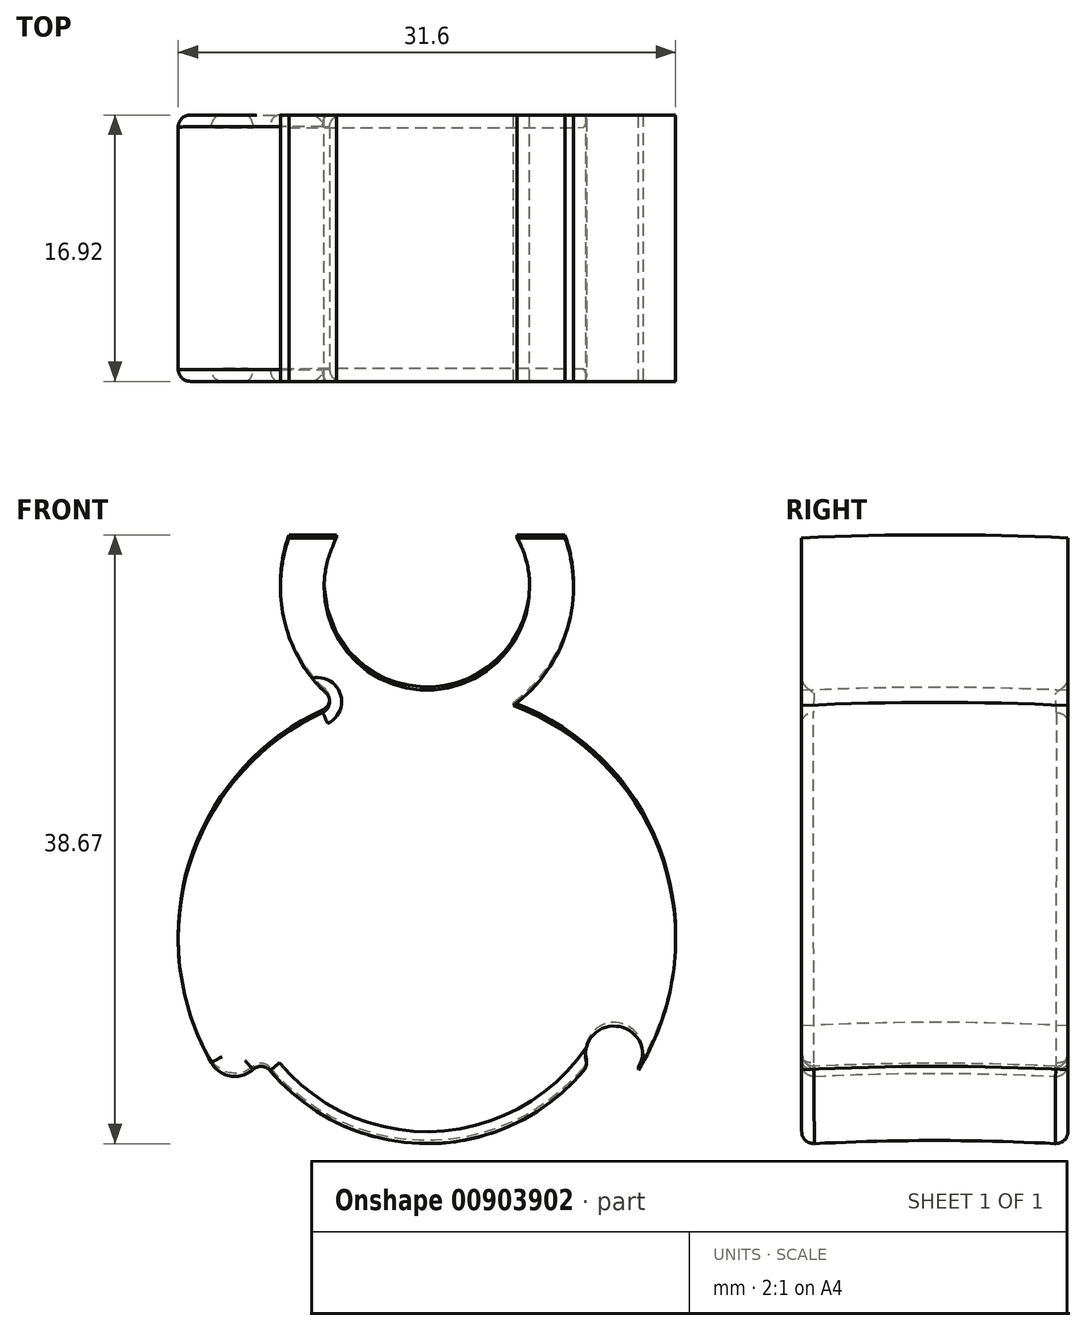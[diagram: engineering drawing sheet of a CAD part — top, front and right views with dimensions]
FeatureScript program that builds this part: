
annotation { "Feature Type Name" : "Feature", "Feature Type Description" : "" }
export const myFeature = defineFeature(function(context is Context, id is Id, definition is map)
    precondition{}
    {
        {
            var Q0;
            Q0=qCreatedBy(makeId("Front.planeOp"),FACE);
            var sketch = newSketch(context, id + "F0", { "sketchPlane" : qUnion([Q0])});
            skCircle(sketch, "E0", {"center": v(0, 35.34) * mm, "radius": 6.53 * mm});
            skCircle(sketch, "E1", {"center": v(0, 13.02) * mm, "radius": 13.02 * mm});
            skCircle(sketch, "E2", {"center": v(0, 13.02) * mm, "radius": 15.8 * mm});
            skCircle(sketch, "E3", {"center": v(0, 35.34) * mm, "radius": 9.3 * mm});
            skLineSegment(sketch, "E4", {"start": v(-8.76, 38.47) * mm, "end": v(8.76, 38.47) * mm});
            skLineSegment(sketch, "E5", {"start": v(14.5, 6.77) * mm, "end": v(-14.5, 6.77) * mm, "construction": true});
            skLineSegment(sketch, "E6", {"start": v(-41.6, -149.23) * mm, "end": v(52.5, -149.23) * mm, "construction": true});
            skCircle(sketch, "E7", {"center": v(-11.42, 6.77) * mm, "radius": 0.64 * mm, "construction": true});
            skCircle(sketch, "E8", {"center": v(11.42, 6.77) * mm, "radius": 0.64 * mm, "construction": true});
            skCircle(sketch, "E9", {"center": v(-12.2, 6) * mm, "radius": 1.73 * mm});
            skCircle(sketch, "E10", {"center": v(11.89, 5.68) * mm, "radius": 1.82 * mm});
            skSolve(sketch);
        }
        {
            var Q0;
            {var subQ0=sQuery(id+"F0.wireOp",EDGE,"E4");var subQ1=sQuery(id+"F0.wireOp",EDGE,"E0");var subQ2=makeQuery(id+"F0.imprint","INTERSECT",VERTEX,{"disambiguationData":[OD(1.0)],"derivedFrom":[subQ1,subQ0]});Q0=makeQuery(id+"F0.imprint","IMPRINT",FACE,{"disambiguationData":[TD([[makeQuery(id+"F0.imprint","IMPRINT",EDGE,{"disambiguationData":[TD([[subQ2,1.0]])],"derivedFrom":subQ1}),-1.0]])]});}
            var Q1;
            {var subQ0=sQuery(id+"F0.wireOp",EDGE,"E3");var subQ1=sQuery(id+"F0.wireOp",EDGE,"E2");var subQ2=makeQuery(id+"F0.imprint","INTERSECT",VERTEX,{"disambiguationData":[OD(0.0)],"derivedFrom":[subQ1,subQ0]});Q1=makeQuery(id+"F0.imprint","IMPRINT",FACE,{"disambiguationData":[TD([[makeQuery(id+"F0.imprint","IMPRINT",EDGE,{"disambiguationData":[TD([[subQ2,-1.0]])],"derivedFrom":subQ1}),1.0]])]});}
            var Q2;
            {var subQ0=sQuery(id+"F0.wireOp",EDGE,"E3");var subQ1=sQuery(id+"F0.wireOp",EDGE,"E1");var subQ2=makeQuery(id+"F0.imprint","INTERSECT",VERTEX,{"derivedFrom":[subQ1,subQ0]});Q2=makeQuery(id+"F0.imprint","IMPRINT",FACE,{"disambiguationData":[TD([[makeQuery(id+"F0.imprint","IMPRINT",EDGE,{"disambiguationData":[TD([[subQ2,1.0]])],"derivedFrom":subQ1}),-1.0]])]});}
            var Q3;
            {var subQ0=sQuery(id+"F0.wireOp",EDGE,"E4");var subQ1=sQuery(id+"F0.wireOp",EDGE,"E0");var subQ2=makeQuery(id+"F0.imprint","INTERSECT",VERTEX,{"disambiguationData":[OD(0.0)],"derivedFrom":[subQ1,subQ0]});Q3=makeQuery(id+"F0.imprint","IMPRINT",FACE,{"disambiguationData":[TD([[makeQuery(id+"F0.imprint","IMPRINT",EDGE,{"disambiguationData":[TD([[subQ2,-1.0]])],"derivedFrom":subQ1}),-1.0]])]});}
            var Q4;
            {var subQ0=sQuery(id+"F0.wireOp",EDGE,"E10");var subQ1=sQuery(id+"F0.wireOp",EDGE,"E1");var subQ2=makeQuery(id+"F0.imprint","INTERSECT",VERTEX,{"disambiguationData":[OD(0.0)],"derivedFrom":[subQ1,subQ0]});Q4=makeQuery(id+"F0.imprint","IMPRINT",FACE,{"disambiguationData":[TD([[makeQuery(id+"F0.imprint","IMPRINT",EDGE,{"disambiguationData":[TD([[subQ2,-1.0]])],"derivedFrom":subQ1}),-1.0]])]});}
            var Q5;
            {var subQ0=sQuery(id+"F0.wireOp",EDGE,"E10");var subQ1=sQuery(id+"F0.wireOp",EDGE,"E1");var subQ2=makeQuery(id+"F0.imprint","INTERSECT",VERTEX,{"disambiguationData":[OD(0.0)],"derivedFrom":[subQ1,subQ0]});Q5=makeQuery(id+"F0.imprint","IMPRINT",FACE,{"disambiguationData":[TD([[makeQuery(id+"F0.imprint","IMPRINT",EDGE,{"disambiguationData":[TD([[subQ2,-1.0]])],"derivedFrom":subQ1}),1.0]])]});}
            var Q6;
            {var subQ0=sQuery(id+"F0.wireOp",EDGE,"E9");var subQ1=sQuery(id+"F0.wireOp",EDGE,"E1");var subQ2=makeQuery(id+"F0.imprint","INTERSECT",VERTEX,{"disambiguationData":[OD(0.0)],"derivedFrom":[subQ1,subQ0]});Q6=makeQuery(id+"F0.imprint","IMPRINT",FACE,{"disambiguationData":[TD([[makeQuery(id+"F0.imprint","IMPRINT",EDGE,{"disambiguationData":[TD([[subQ2,1.0]])],"derivedFrom":subQ1}),-1.0]])]});}
            var Q7;
            {var subQ0=sQuery(id+"F0.wireOp",EDGE,"E9");var subQ1=sQuery(id+"F0.wireOp",EDGE,"E1");var subQ2=makeQuery(id+"F0.imprint","INTERSECT",VERTEX,{"disambiguationData":[OD(0.0)],"derivedFrom":[subQ1,subQ0]});Q7=makeQuery(id+"F0.imprint","IMPRINT",FACE,{"disambiguationData":[TD([[makeQuery(id+"F0.imprint","IMPRINT",EDGE,{"disambiguationData":[TD([[subQ2,-1.0]])],"derivedFrom":subQ1}),-1.0]])]});}
            var Q8;
            {var subQ0=sQuery(id+"F0.wireOp",EDGE,"E9");var subQ1=sQuery(id+"F0.wireOp",EDGE,"E1");var subQ2=makeQuery(id+"F0.imprint","INTERSECT",VERTEX,{"disambiguationData":[OD(0.0)],"derivedFrom":[subQ1,subQ0]});Q8=makeQuery(id+"F0.imprint","IMPRINT",FACE,{"disambiguationData":[TD([[makeQuery(id+"F0.imprint","IMPRINT",EDGE,{"disambiguationData":[TD([[subQ2,-1.0]])],"derivedFrom":subQ1}),1.0]])]});}
            var Q9;
            Q9=sQuery(id+"F0.wireOp",EDGE,"E6");
            revolve(context, id + "F1", {"surfaceOperationType" : NewSurfaceOperationType.NEW, "entities" : qUnion([Q0, Q1, Q2, Q3, Q4, Q5, Q6, Q7, Q8]), "axis" : qUnion([Q9]), "revolveType" : RevolveType.SYMMETRIC, "angle" : 10 * degree});
        }
        {
            var Q0;
            Q0=qCreatedBy(makeId("Right.planeOp"),FACE);
            var sketch = newSketch(context, id + "F2", { "sketchPlane" : qUnion([Q0])});
            skLineSegment(sketch, "E11.bottom", {"start": v(8.46, 63.5) * mm, "end": v(-8.46, 63.5) * mm});
            skLineSegment(sketch, "E11.top", {"start": v(8.46, -63.5) * mm, "end": v(-8.46, -63.5) * mm});
            skLineSegment(sketch, "E11.left", {"start": v(8.46, 63.5) * mm, "end": v(8.46, -63.5) * mm});
            skLineSegment(sketch, "E11.right", {"start": v(-8.46, 63.5) * mm, "end": v(-8.46, -63.5) * mm});
            skPoint(sketch, "E11.middle", {"position": v(0, 0) * mm});
            skSolve(sketch);
        }
        {
            var Q0;
            Q0=makeQuery(id+"F2.imprint","IMPRINT",FACE,{"disambiguationData":[TD([[makeQuery(id+"F2.imprint","IMPRINT",EDGE,{"derivedFrom":sQuery(id+"F2.wireOp",EDGE,"E11.bottom")}),1.0]])]});
            extrude(context, id + "F3", {"entities" : qUnion([Q0]), "operationType" : NewBodyOperationType.INTERSECT, "endBound" : BoundingType.SYMMETRIC, "depth" : 38.1 * mm, "offsetDistance" : 25.4 * mm});
        }
        {
            var Q0;
            {var subQ0=sQuery(id+"F0.wireOp",EDGE,"E2");Q0=makeQuery(id+"F1.opRevolve","SWEPT_FACE",FACE,{"disambiguationData":[OSD([subQ0]),TDD([makeQuery(id+"F0.imprint","IMPRINT",EDGE,{"disambiguationData":[TD([[makeQuery(id+"F0.imprint","INTERSECT",VERTEX,{"disambiguationData":[OD(1.0)],"derivedFrom":[subQ0,sQuery(id+"F0.wireOp",EDGE,"E3")]}),-1.0]])],"derivedFrom":subQ0})])]});}
            var Q1;
            {var subQ0=sQuery(id+"F0.wireOp",EDGE,"E3");Q1=makeQuery(id+"F1.opRevolve","SWEPT_FACE",FACE,{"disambiguationData":[OSD([subQ0]),TDD([makeQuery(id+"F0.imprint","IMPRINT",EDGE,{"disambiguationData":[TD([[makeQuery(id+"F0.imprint","INTERSECT",VERTEX,{"disambiguationData":[OD(0.0)],"derivedFrom":[subQ0,sQuery(id+"F0.wireOp",EDGE,"E4")]}),-1.0]])],"derivedFrom":subQ0})])]});}
            var Q2;
            Q2=makeQuery(id+"F3.boolean.opBoolean","COPY",FACE,{"derivedFrom":makeQuery(id+"F3.boolean.toolComplement.opBoolean","COPY",FACE,{"derivedFrom":makeQuery(id+"F3.opExtrude","SWEPT_FACE",FACE,{"disambiguationData":[OSD([sQuery(id+"F2.wireOp",EDGE,"E11.right")])]})})});
            var Q3;
            Q3=makeQuery(id+"F1.opRevolve","SWEPT_FACE",FACE,{"disambiguationData":[OSD([sQuery(id+"F0.wireOp",EDGE,"E1")])]});
            var Q4;
            {var subQ0=sQuery(id+"F0.wireOp",EDGE,"E4");Q4=makeQuery(id+"F3.boolean.opBoolean","INTERSECT",EDGE,{"derivedFrom":[makeQuery(id+"F1.opRevolve","SWEPT_FACE",FACE,{"disambiguationData":[OSD([subQ0]),TDD([makeQuery(id+"F0.imprint","IMPRINT",EDGE,{"disambiguationData":[TD([[makeQuery(id+"F0.imprint","INTERSECT",VERTEX,{"disambiguationData":[OD(0.0)],"derivedFrom":[sQuery(id+"F0.wireOp",EDGE,"E3"),subQ0]}),-1.0]])],"derivedFrom":subQ0})])]}),makeQuery(id+"F3.boolean.toolComplement.opBoolean","COPY",FACE,{"derivedFrom":makeQuery(id+"F3.opExtrude","SWEPT_FACE",FACE,{"disambiguationData":[OSD([sQuery(id+"F2.wireOp",EDGE,"E11.left")])]})})]});}
            var Q5;
            {var subQ0=sQuery(id+"F0.wireOp",EDGE,"E4");Q5=makeQuery(id+"F1.opRevolve","SWEPT_FACE",FACE,{"disambiguationData":[OSD([subQ0]),TDD([makeQuery(id+"F0.imprint","IMPRINT",EDGE,{"disambiguationData":[TD([[makeQuery(id+"F0.imprint","INTERSECT",VERTEX,{"disambiguationData":[OD(1.0)],"derivedFrom":[sQuery(id+"F0.wireOp",EDGE,"E3"),subQ0]}),1.0]])],"derivedFrom":subQ0})])]});}
            var Q6;
            {var subQ0=sQuery(id+"F0.wireOp",EDGE,"E4");Q6=makeQuery(id+"F1.opRevolve","SWEPT_FACE",FACE,{"disambiguationData":[OSD([subQ0]),TDD([makeQuery(id+"F0.imprint","IMPRINT",EDGE,{"disambiguationData":[TD([[makeQuery(id+"F0.imprint","INTERSECT",VERTEX,{"disambiguationData":[OD(0.0)],"derivedFrom":[sQuery(id+"F0.wireOp",EDGE,"E3"),subQ0]}),-1.0]])],"derivedFrom":subQ0})])]});}
            var Q7;
            Q7=makeQuery(id+"F3.boolean.opBoolean","COPY",FACE,{"derivedFrom":makeQuery(id+"F3.boolean.toolComplement.opBoolean","COPY",FACE,{"derivedFrom":makeQuery(id+"F3.opExtrude","SWEPT_FACE",FACE,{"disambiguationData":[OSD([sQuery(id+"F2.wireOp",EDGE,"E11.left")])]})})});
            var Q8;
            {var subQ0=sQuery(id+"F0.wireOp",EDGE,"E3");Q8=makeQuery(id+"F1.opRevolve","SWEPT_FACE",FACE,{"disambiguationData":[OSD([subQ0]),TDD([makeQuery(id+"F0.imprint","IMPRINT",EDGE,{"disambiguationData":[TD([[makeQuery(id+"F0.imprint","INTERSECT",VERTEX,{"disambiguationData":[OD(1.0)],"derivedFrom":[subQ0,sQuery(id+"F0.wireOp",EDGE,"E4")]}),1.0]])],"derivedFrom":subQ0})])]});}
            fillet(context, id + "F4", {"entities" : qUnion([Q0, Q1, Q2, Q3, Q4, Q5, Q6, Q7, Q8]), "radius" : 0.76 * mm, "tangentPropagation" : true, "allowEdgeOverflow" : false});
        }
    });
